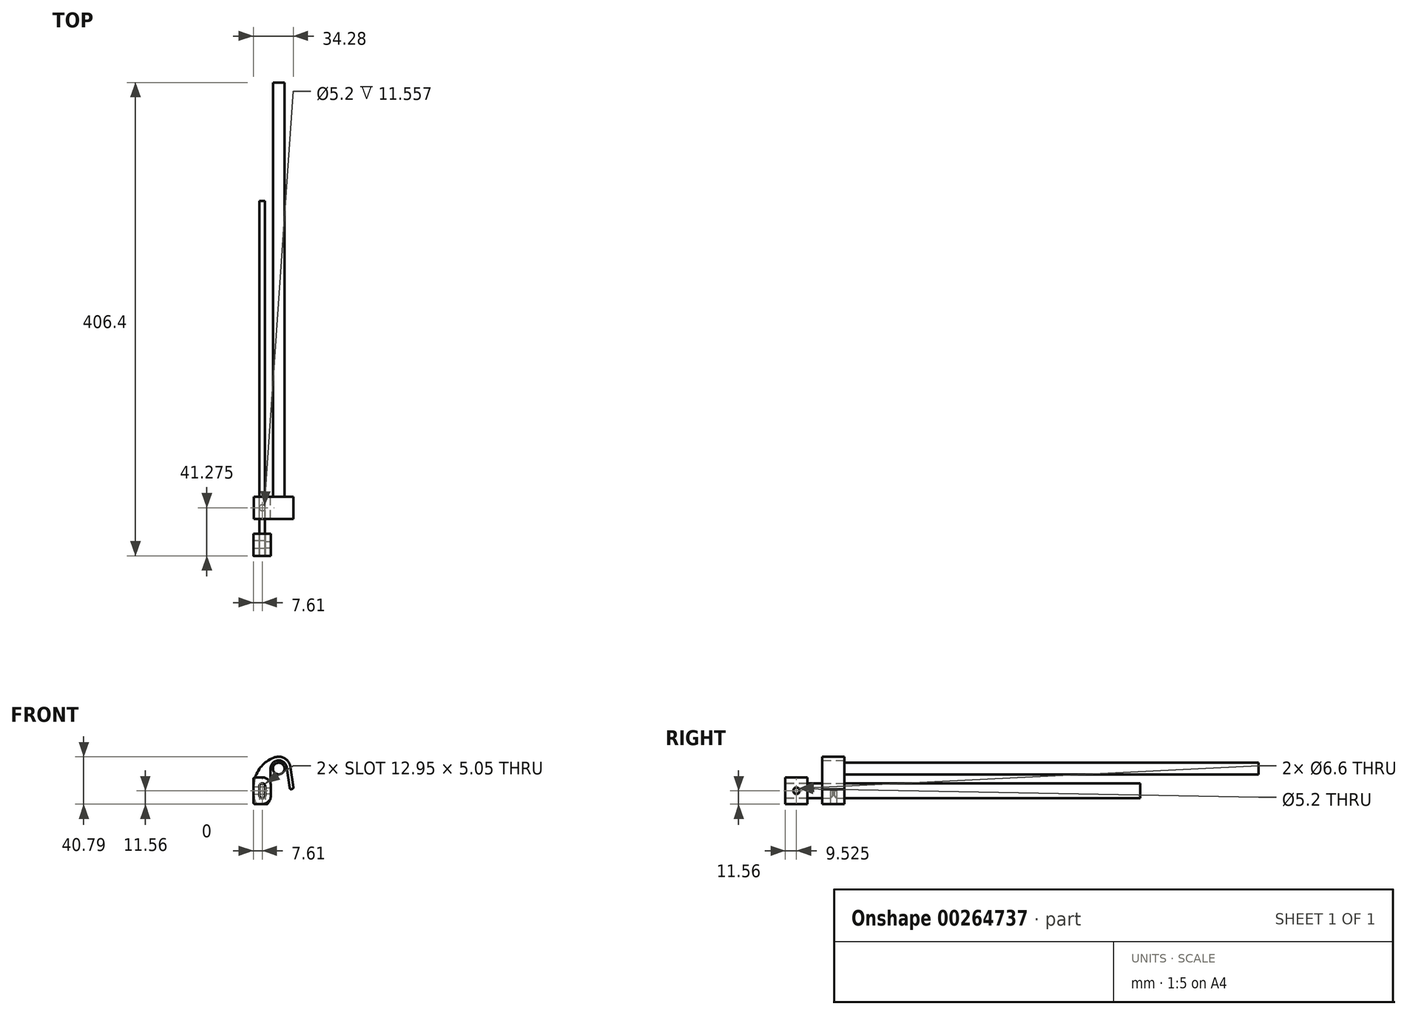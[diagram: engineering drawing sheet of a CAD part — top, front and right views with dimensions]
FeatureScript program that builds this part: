
annotation { "Feature Type Name" : "Feature", "Feature Type Description" : "" }
export const myFeature = defineFeature(function(context is Context, id is Id, definition is map)
    precondition{}
    {
        {
            var Q0;
            Q0=qCreatedBy(makeId("Front.planeOp"),FACE);
            var sketch = newSketch(context, id + "F0", { "sketchPlane" : qUnion([Q0])});
            skLineSegment(sketch, "E0.bottom", {"start": v(2.4, -3.95) * mm, "end": v(-2.4, -3.95) * mm, "construction": true});
            skLineSegment(sketch, "E0.top", {"start": v(2.4, 3.95) * mm, "end": v(-2.4, 3.95) * mm, "construction": true});
            skLineSegment(sketch, "E0.left", {"start": v(2.4, -3.95) * mm, "end": v(2.4, 3.95) * mm});
            skLineSegment(sketch, "E0.right", {"start": v(-2.4, -3.95) * mm, "end": v(-2.4, 3.95) * mm});
            skPoint(sketch, "E0.middle", {"position": v(0, 0) * mm});
            skArc(sketch, "E1", {"start": v(2.4, 3.95) * mm, "mid": v(0, 6.35) * mm, "end": v(-2.4, 3.95) * mm});
            skArc(sketch, "E2", {"start": v(-2.4, -3.95) * mm, "mid": v(0, -6.35) * mm, "end": v(2.4, -3.95) * mm});
            skSolve(sketch);
        }
        {
            var Q0;
            Q0=qSketchRegion(id+"F0",true);
            extrude(context, id + "F1", {"entities" : qUnion([Q0]), "depth" : 304.8 * mm, "symmetric" : true});
        }
        {
            var Q0;
            Q0=makeQuery(id+"F1.opExtrude","CAP_FACE",FACE,{"disambiguationData":[OSD([sQuery(id+"F0.wireOp",EDGE,"E0.left"),sQuery(id+"F0.wireOp",EDGE,"E0.right"),sQuery(id+"F0.wireOp",EDGE,"E1"),sQuery(id+"F0.wireOp",EDGE,"E2")])],"isStart":false});
            var sketch = newSketch(context, id + "F2", { "sketchPlane" : qUnion([Q0])});
            skArc(sketch, "E3.0", {"start": v(2.53, 3.95) * mm, "mid": v(0, 6.48) * mm, "end": v(-2.53, 3.95) * mm});
            skLineSegment(sketch, "E3.1", {"start": v(2.53, -3.95) * mm, "end": v(2.53, 3.95) * mm});
            skArc(sketch, "E3.2", {"start": v(-2.53, -3.95) * mm, "mid": v(0, -6.48) * mm, "end": v(2.53, -3.95) * mm});
            skLineSegment(sketch, "E3.3", {"start": v(-2.53, -3.95) * mm, "end": v(-2.53, 3.95) * mm});
            skArc(sketch, "E4.0", {"start": v(7.48, 3.95) * mm, "mid": v(5.29, 9.24) * mm, "end": v(0, 11.43) * mm});
            skLineSegment(sketch, "E4.1", {"start": v(7.48, -3.95) * mm, "end": v(7.48, 3.95) * mm});
            skArc(sketch, "E4.2", {"start": v(0, -11.43) * mm, "mid": v(5.29, -9.24) * mm, "end": v(7.48, -3.95) * mm});
            skLineSegment(sketch, "E5", {"start": v(-7.6, 11.43) * mm, "end": v(-7.6, -11.43) * mm});
            skLineSegment(sketch, "E6", {"start": v(0, 11.43) * mm, "end": v(-7.6, 11.43) * mm});
            skLineSegment(sketch, "E7", {"start": v(0, -11.43) * mm, "end": v(-7.6, -11.43) * mm});
            skSolve(sketch);
        }
        {
            var Q0;
            Q0=qSketchRegion(id+"F2",true);
            extrude(context, id + "F3", {"entities" : qUnion([Q0]), "oppositeDirection" : true, "depth" : 19.05 * mm});
        }
        {
            var Q0;
            Q0=makeQuery(id+"F3.opExtrude","SWEPT_FACE",FACE,{"disambiguationData":[OSD([sQuery(id+"F2.wireOp",EDGE,"E4.1")])]});
            var sketch = newSketch(context, id + "F4", { "sketchPlane" : qUnion([Q0])});
            skLineSegment(sketch, "E8", {"start": v(-152.4, 3.95) * mm, "end": v(-133.35, -3.95) * mm, "construction": true});
            skCircle(sketch, "E9", {"center": v(-142.88, 0) * mm, "radius": 2.6 * mm});
            skSolve(sketch);
        }
        {
            var Q0;
            Q0=qSketchRegion(id+"F4",true);
            extrude(context, id + "F5", {"entities" : qUnion([Q0]), "operationType" : NewBodyOperationType.REMOVE, "endBound" : BoundingType.THROUGH_ALL, "oppositeDirection" : true, "depth" : 25.4 * mm});
        }
        {
            var Q0;
            Q0=makeQuery(id+"F3.opExtrude","SWEPT_FACE",FACE,{"disambiguationData":[OSD([sQuery(id+"F2.wireOp",EDGE,"E5")])]});
            var sketch = newSketch(context, id + "F6", { "sketchPlane" : qUnion([Q0])});
            skCircle(sketch, "E10", {"center": v(142.88, 0) * mm, "radius": 3.3 * mm});
            skSolve(sketch);
        }
        {
            var Q0;
            Q0=qSketchRegion(id+"F6",true);
            var Q1;
            Q1=makeQuery(id+"F1.opExtrude","SWEPT_FACE",FACE,{"disambiguationData":[OSD([sQuery(id+"F0.wireOp",EDGE,"E0.left")])]});
            extrude(context, id + "F7", {"entities" : qUnion([Q0]), "operationType" : NewBodyOperationType.REMOVE, "endBound" : BoundingType.UP_TO_SURFACE, "oppositeDirection" : true, "endBoundEntityFace" : qUnion([Q1]), "depth" : 25.4 * mm});
        }
        {
            var Q0;
            Q0=qCreatedBy(makeId("Front.planeOp"),FACE);
            cPlane(context, id + "F8", {"entities" : qUnion([Q0]), "cplaneType" : CPlaneType.OFFSET, "offset" : 101.6 * mm, "width" : 152.4 * mm, "height" : 152.4 * mm});
        }
        {
            var Q0;
            Q0=qCreatedBy(id+"F8.planeOp",FACE);
            var sketch = newSketch(context, id + "F9", { "sketchPlane" : qUnion([Q0])});
            skArc(sketch, "E11.0", {"start": v(2.53, 3.95) * mm, "mid": v(0, 6.48) * mm, "end": v(-2.53, 3.95) * mm});
            skLineSegment(sketch, "E12.0", {"start": v(-2.53, -3.95) * mm, "end": v(-2.53, 3.95) * mm});
            skLineSegment(sketch, "E13.0", {"start": v(2.53, -3.95) * mm, "end": v(2.53, 3.95) * mm});
            skArc(sketch, "E14.0", {"start": v(-2.53, -3.95) * mm, "mid": v(0, -6.48) * mm, "end": v(2.53, -3.95) * mm});
            skArc(sketch, "E15.0", {"start": v(7.1, 3.95) * mm, "mid": v(0, 11.05) * mm, "end": v(-7.1, 3.95) * mm, "construction": true});
            skLineSegment(sketch, "E15.1", {"start": v(7.1, -3.95) * mm, "end": v(7.1, 3.95) * mm});
            skArc(sketch, "E15.2", {"start": v(-7.1, -3.95) * mm, "mid": v(0, -11.05) * mm, "end": v(7.1, -3.95) * mm, "construction": true});
            skLineSegment(sketch, "E15.3", {"start": v(-7.1, -3.95) * mm, "end": v(-7.1, 3.95) * mm});
            skLineSegment(sketch, "E16", {"start": v(-4.45, -11.56) * mm, "end": v(4.45, -11.56) * mm});
            skArc(sketch, "E17", {"start": v(-7.1, -3.95) * mm, "mid": v(-6.42, -7.98) * mm, "end": v(-4.44, -11.56) * mm});
            skArc(sketch, "E18", {"start": v(4.45, -11.56) * mm, "mid": v(6.42, -7.98) * mm, "end": v(7.1, -3.95) * mm});
            skLineSegment(sketch, "E19", {"start": v(7.1, 3.95) * mm, "end": v(7.1, 19.05) * mm});
            skLineSegment(sketch, "E20", {"start": v(7.1, 19.05) * mm, "end": v(21.04, 20.02) * mm, "construction": true});
            skLineSegment(sketch, "E21", {"start": v(7.1, 19.05) * mm, "end": v(16.59, 19.05) * mm, "construction": true});
            skArc(sketch, "E22", {"start": v(21.04, 20.02) * mm, "mid": v(13.61, 26.04) * mm, "end": v(7.1, 19.05) * mm});
            skLineSegment(sketch, "E23", {"start": v(21.04, 20.02) * mm, "end": v(23.69, 1.16) * mm});
            skLineSegment(sketch, "E24.0", {"start": v(24.18, 20.47) * mm, "end": v(26.83, 1.6) * mm});
            skArc(sketch, "E24.1", {"start": v(24.18, 20.47) * mm, "mid": v(19.51, 27.67) * mm, "end": v(11, 28.74) * mm});
            skArc(sketch, "E25", {"start": v(11, 28.74) * mm, "mid": v(-2.1, 19.3) * mm, "end": v(-7.1, 3.95) * mm});
            skLineSegment(sketch, "E26", {"start": v(23.69, 1.16) * mm, "end": v(26.83, 1.6) * mm});
            skSolve(sketch);
        }
        {
            var Q0;
            Q0=qSketchRegion(id+"F9",true);
            extrude(context, id + "F10", {"entities" : qUnion([Q0]), "depth" : 19.05 * mm});
        }
        {
            var Q0;
            Q0=makeQuery(id+"F10.opExtrude","SWEPT_EDGE",EDGE,{"disambiguationData":[OSD([sQuery(id+"F9.wireOp",EDGE,"E24.0"),sQuery(id+"F9.wireOp",EDGE,"E26")])]});
            var Q1;
            Q1=makeQuery(id+"F10.opExtrude","SWEPT_EDGE",EDGE,{"disambiguationData":[OSD([sQuery(id+"F9.wireOp",EDGE,"E23"),sQuery(id+"F9.wireOp",EDGE,"E26")])]});
            var Q2;
            Q2=makeQuery(id+"F10.opExtrude","SWEPT_EDGE",EDGE,{"disambiguationData":[OSD([sQuery(id+"F9.wireOp",EDGE,"E16"),sQuery(id+"F9.wireOp",EDGE,"E17")])]});
            var Q3;
            Q3=makeQuery(id+"F10.opExtrude","SWEPT_EDGE",EDGE,{"disambiguationData":[OSD([sQuery(id+"F9.wireOp",EDGE,"E16"),sQuery(id+"F9.wireOp",EDGE,"E18")])]});
            var Q4;
            Q4=makeQuery(id+"F3.opExtrude","SWEPT_EDGE",EDGE,{"disambiguationData":[OSD([sQuery(id+"F2.wireOp",EDGE,"E5"),sQuery(id+"F2.wireOp",EDGE,"E7")])]});
            var Q5;
            Q5=makeQuery(id+"F3.opExtrude","SWEPT_EDGE",EDGE,{"disambiguationData":[OSD([sQuery(id+"F2.wireOp",EDGE,"E5"),sQuery(id+"F2.wireOp",EDGE,"E6")])]});
            fillet(context, id + "F11", {"entities" : qUnion([Q0, Q1, Q2, Q3, Q4, Q5]), "radius" : 1.27 * mm, "tangentPropagation" : true, "allowEdgeOverflow" : false});
        }
        {
            var Q0;
            Q0=makeQuery(id+"F10.opExtrude","SWEPT_FACE",FACE,{"disambiguationData":[OSD([sQuery(id+"F9.wireOp",EDGE,"E16")])]});
            var sketch = newSketch(context, id + "F12", { "sketchPlane" : qUnion([Q0])});
            skLineSegment(sketch, "E27", {"start": v(-3.81, 120.65) * mm, "end": v(3.81, 101.6) * mm, "construction": true});
            skCircle(sketch, "E28", {"center": v(0, 111.12) * mm, "radius": 2.6 * mm});
            skSolve(sketch);
        }
        {
            var Q0;
            Q0=qSketchRegion(id+"F12",true);
            var Q1;
            Q1=qCreatedBy(makeId("Top.planeOp"),FACE);
            extrude(context, id + "F13", {"entities" : qUnion([Q0]), "operationType" : NewBodyOperationType.REMOVE, "endBound" : BoundingType.UP_TO_SURFACE, "oppositeDirection" : true, "endBoundEntityFace" : qUnion([Q1]), "depth" : 25.4 * mm});
        }
        {
            var Q0;
            Q0=makeQuery(id+"F10.opExtrude","CAP_FACE",FACE,{"disambiguationData":[OSD([sQuery(id+"F9.wireOp",EDGE,"E11.0"),sQuery(id+"F9.wireOp",EDGE,"E12.0"),sQuery(id+"F9.wireOp",EDGE,"E13.0"),sQuery(id+"F9.wireOp",EDGE,"E14.0"),sQuery(id+"F9.wireOp",EDGE,"E15.1"),sQuery(id+"F9.wireOp",EDGE,"E15.3"),sQuery(id+"F9.wireOp",EDGE,"E16"),sQuery(id+"F9.wireOp",EDGE,"E17"),sQuery(id+"F9.wireOp",EDGE,"E18"),sQuery(id+"F9.wireOp",EDGE,"E19"),sQuery(id+"F9.wireOp",EDGE,"E22"),sQuery(id+"F9.wireOp",EDGE,"E23"),sQuery(id+"F9.wireOp",EDGE,"E24.0"),sQuery(id+"F9.wireOp",EDGE,"E24.1"),sQuery(id+"F9.wireOp",EDGE,"E25"),sQuery(id+"F9.wireOp",EDGE,"E26")])],"isStart":true});
            var sketch = newSketch(context, id + "F14", { "sketchPlane" : qUnion([Q0])});
            skCircle(sketch, "E29", {"center": v(-14.1, 19.05) * mm, "radius": 5 * mm});
            skSolve(sketch);
        }
        {
            var Q0;
            Q0=qSketchRegion(id+"F14",true);
            extrude(context, id + "F15", {"entities" : qUnion([Q0]), "depth" : 355.6 * mm, "offsetDistance" : 25.4 * mm});
        }
    });
